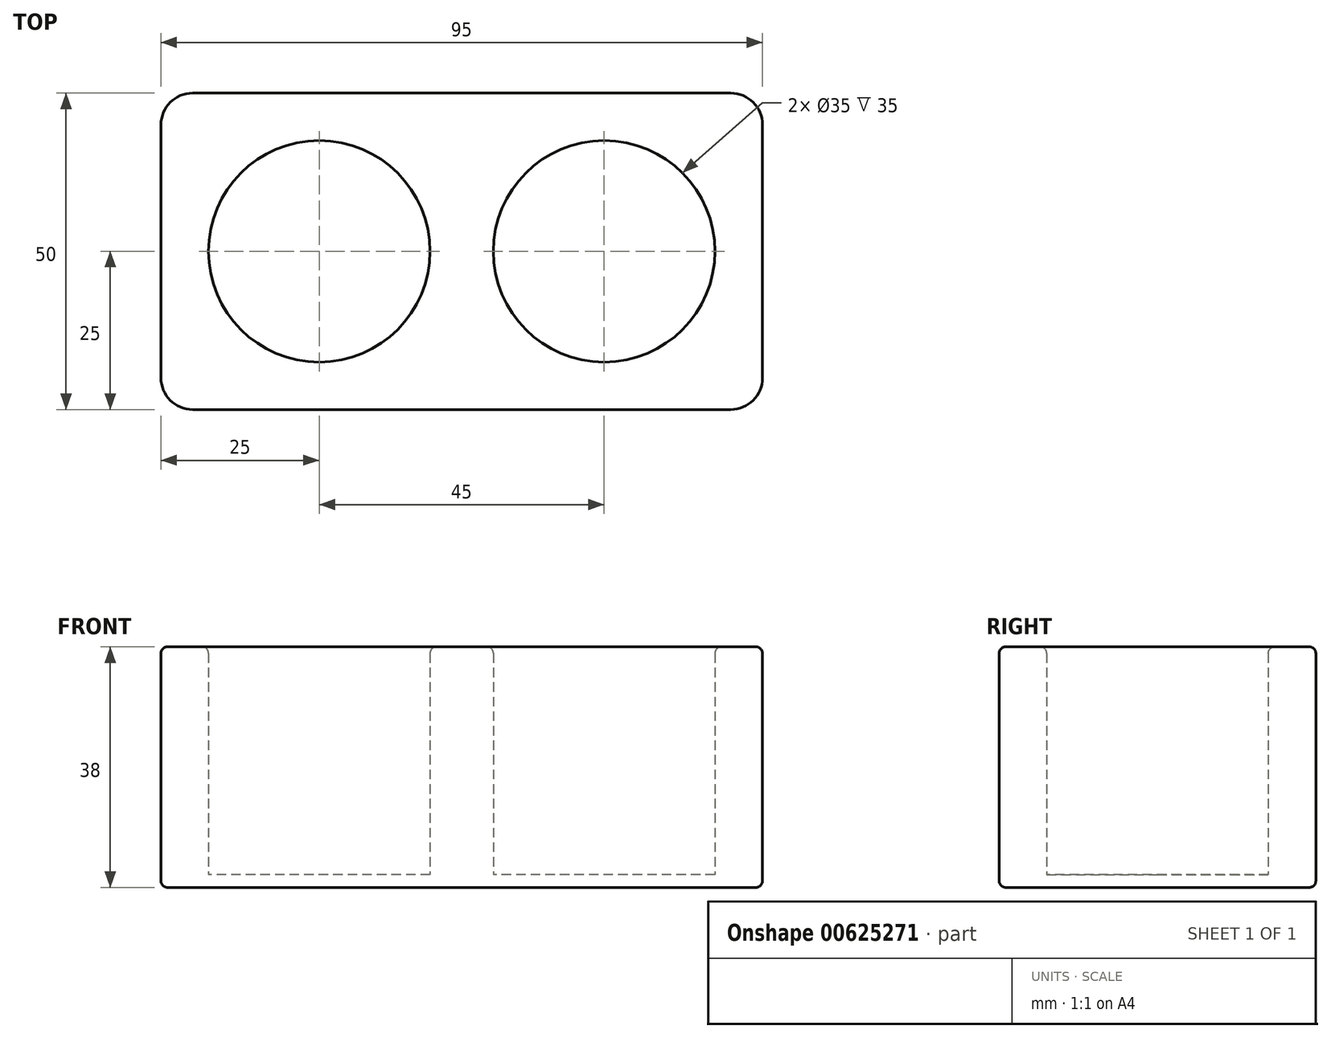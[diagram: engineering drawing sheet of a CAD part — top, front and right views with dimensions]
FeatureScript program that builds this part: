
annotation { "Feature Type Name" : "Feature", "Feature Type Description" : "" }
export const myFeature = defineFeature(function(context is Context, id is Id, definition is map)
    precondition{}
    {
        {
            var Q0;
            Q0=qCreatedBy(makeId("Top.planeOp"),FACE);
            var sketch = newSketch(context, id + "F0", { "sketchPlane" : qUnion([Q0])});
            skLineSegment(sketch, "E0.bottom", {"start": v(-47.5, 25) * mm, "end": v(47.5, 25) * mm});
            skLineSegment(sketch, "E0.top", {"start": v(-47.5, -25) * mm, "end": v(47.5, -25) * mm});
            skLineSegment(sketch, "E0.left", {"start": v(-47.5, 25) * mm, "end": v(-47.5, -25) * mm});
            skLineSegment(sketch, "E0.right", {"start": v(47.5, 25) * mm, "end": v(47.5, -25) * mm});
            skPoint(sketch, "E0.middle", {"position": v(0, 0) * mm});
            skCircle(sketch, "E1", {"center": v(-22.5, 0) * mm, "radius": 17.5 * mm});
            skCircle(sketch, "E2", {"center": v(22.5, 0) * mm, "radius": 17.5 * mm});
            skSolve(sketch);
        }
        {
            var Q0;
            Q0=qSketchRegion(id+"F0",true);
            var Q1;
            Q1=makeQuery(id+"F0.imprint","IMPRINT",FACE,{"disambiguationData":[TD([[makeQuery(id+"F0.imprint","IMPRINT",EDGE,{"derivedFrom":sQuery(id+"F0.wireOp",EDGE,"E0.bottom")}),-1.0]])]});
            extrude(context, id + "F1", {"entities" : qUnion([Q0, Q1]), "depth" : 36 * mm, "offsetDistance" : 25 * mm});
        }
        {
            var Q0;
            Q0=makeQuery(id+"F1.opExtrude","CAP_FACE",FACE,{"disambiguationData":[OSD([sQuery(id+"F0.wireOp",EDGE,"E0.bottom"),sQuery(id+"F0.wireOp",EDGE,"E0.top"),sQuery(id+"F0.wireOp",EDGE,"E0.left"),sQuery(id+"F0.wireOp",EDGE,"E0.right"),sQuery(id+"F0.wireOp",EDGE,"E1"),sQuery(id+"F0.wireOp",EDGE,"E2")])],"isStart":true});
            var sketch = newSketch(context, id + "F2", { "sketchPlane" : qUnion([Q0])});
            skLineSegment(sketch, "E3.bottom", {"start": v(47.5, -25) * mm, "end": v(-47.5, -25) * mm});
            skLineSegment(sketch, "E3.top", {"start": v(47.5, 25) * mm, "end": v(-47.5, 25) * mm});
            skLineSegment(sketch, "E3.left", {"start": v(47.5, -25) * mm, "end": v(47.5, 25) * mm});
            skLineSegment(sketch, "E3.right", {"start": v(-47.5, -25) * mm, "end": v(-47.5, 25) * mm});
            skSolve(sketch);
        }
        {
            var Q0;
            Q0=qSketchRegion(id+"F2",true);
            extrude(context, id + "F3", {"entities" : qUnion([Q0]), "operationType" : NewBodyOperationType.ADD, "depth" : 2 * mm, "offsetDistance" : 25 * mm});
        }
        {
            var Q0;
            Q0=makeQuery(id+"F1.opExtrude","CAP_FACE",FACE,{"disambiguationData":[OSD([sQuery(id+"F0.wireOp",EDGE,"E0.bottom"),sQuery(id+"F0.wireOp",EDGE,"E0.top"),sQuery(id+"F0.wireOp",EDGE,"E0.left"),sQuery(id+"F0.wireOp",EDGE,"E0.right"),sQuery(id+"F0.wireOp",EDGE,"E1"),sQuery(id+"F0.wireOp",EDGE,"E2")])],"isStart":false});
            var Q1;
            Q1=makeQuery(id+"F3.opExtrude","CAP_FACE",FACE,{"disambiguationData":[OSD([sQuery(id+"F2.wireOp",EDGE,"E3.bottom"),sQuery(id+"F2.wireOp",EDGE,"E3.top"),sQuery(id+"F2.wireOp",EDGE,"E3.left"),sQuery(id+"F2.wireOp",EDGE,"E3.right")])],"isStart":false});
            fillet(context, id + "F4", {"entities" : qUnion([Q0, Q1]), "radius" : 1 * mm, "tangentPropagation" : true, "allowEdgeOverflow" : false});
        }
        {
            var Q0;
            Q0=makeQuery(id+"F3.boolean.opBoolean","MERGE",EDGE,{"derivedFrom":[makeQuery(id+"F1.opExtrude","SWEPT_EDGE",EDGE,{"disambiguationData":[OSD([sQuery(id+"F0.wireOp",EDGE,"E0.bottom"),sQuery(id+"F0.wireOp",EDGE,"E0.right")])]}),makeQuery(id+"F3.opExtrude","SWEPT_EDGE",EDGE,{"disambiguationData":[OSD([sQuery(id+"F2.wireOp",EDGE,"E3.bottom"),sQuery(id+"F2.wireOp",EDGE,"E3.left")])]})]});
            var Q1;
            Q1=makeQuery(id+"F3.boolean.opBoolean","MERGE",EDGE,{"derivedFrom":[makeQuery(id+"F1.opExtrude","SWEPT_EDGE",EDGE,{"disambiguationData":[OSD([sQuery(id+"F0.wireOp",EDGE,"E0.top"),sQuery(id+"F0.wireOp",EDGE,"E0.right")])]}),makeQuery(id+"F3.opExtrude","SWEPT_EDGE",EDGE,{"disambiguationData":[OSD([sQuery(id+"F2.wireOp",EDGE,"E3.top"),sQuery(id+"F2.wireOp",EDGE,"E3.left")])]})]});
            var Q2;
            Q2=makeQuery(id+"F3.boolean.opBoolean","MERGE",EDGE,{"derivedFrom":[makeQuery(id+"F1.opExtrude","SWEPT_EDGE",EDGE,{"disambiguationData":[OSD([sQuery(id+"F0.wireOp",EDGE,"E0.top"),sQuery(id+"F0.wireOp",EDGE,"E0.left")])]}),makeQuery(id+"F3.opExtrude","SWEPT_EDGE",EDGE,{"disambiguationData":[OSD([sQuery(id+"F2.wireOp",EDGE,"E3.top"),sQuery(id+"F2.wireOp",EDGE,"E3.right")])]})]});
            var Q3;
            Q3=makeQuery(id+"F3.boolean.opBoolean","MERGE",EDGE,{"derivedFrom":[makeQuery(id+"F1.opExtrude","SWEPT_EDGE",EDGE,{"disambiguationData":[OSD([sQuery(id+"F0.wireOp",EDGE,"E0.bottom"),sQuery(id+"F0.wireOp",EDGE,"E0.left")])]}),makeQuery(id+"F3.opExtrude","SWEPT_EDGE",EDGE,{"disambiguationData":[OSD([sQuery(id+"F2.wireOp",EDGE,"E3.bottom"),sQuery(id+"F2.wireOp",EDGE,"E3.right")])]})]});
            fillet(context, id + "F5", {"entities" : qUnion([Q0, Q1, Q2, Q3]), "radius" : 5 * mm, "tangentPropagation" : true, "allowEdgeOverflow" : false});
        }
    });
